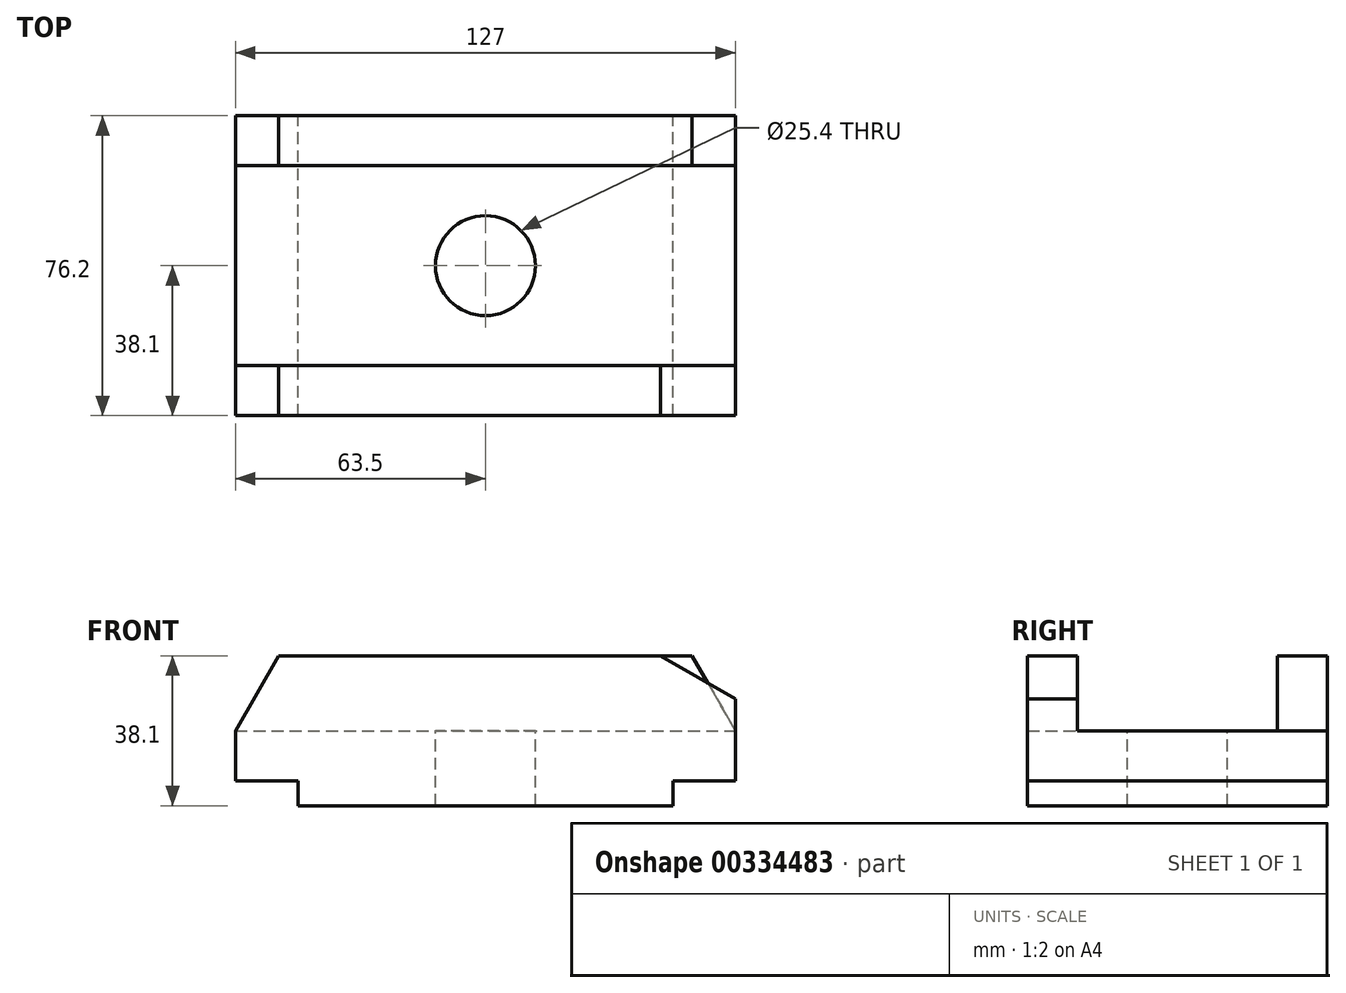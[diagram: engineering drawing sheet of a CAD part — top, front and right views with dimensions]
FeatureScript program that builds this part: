
annotation { "Feature Type Name" : "Feature", "Feature Type Description" : "" }
export const myFeature = defineFeature(function(context is Context, id is Id, definition is map)
    precondition{}
    {
        {
            var Q0;
            Q0=qCreatedBy(makeId("Front.planeOp"),FACE);
            var sketch = newSketch(context, id + "F0", { "sketchPlane" : qUnion([Q0])});
            skLineSegment(sketch, "E0", {"start": v(15.87, 0) * mm, "end": v(111.12, 0) * mm});
            skLineSegment(sketch, "E1", {"start": v(111.12, 0) * mm, "end": v(111.12, 6.35) * mm});
            skLineSegment(sketch, "E2", {"start": v(15.87, 0) * mm, "end": v(15.87, 6.35) * mm});
            skLineSegment(sketch, "E3", {"start": v(15.87, 6.35) * mm, "end": v(0, 6.35) * mm});
            skLineSegment(sketch, "E4", {"start": v(0, 6.35) * mm, "end": v(0, 19.05) * mm});
            skLineSegment(sketch, "E5", {"start": v(111.12, 6.35) * mm, "end": v(127, 6.35) * mm});
            skLineSegment(sketch, "E6", {"start": v(127, 6.35) * mm, "end": v(127, 19.05) * mm});
            skLineSegment(sketch, "E7", {"start": v(127, 19.05) * mm, "end": v(127, 38.1) * mm});
            skLineSegment(sketch, "E8", {"start": v(127, 38.1) * mm, "end": v(0, 38.1) * mm});
            skLineSegment(sketch, "E9", {"start": v(0, 38.1) * mm, "end": v(0, 19.05) * mm});
            skSolve(sketch);
        }
        {
            var Q0;
            Q0=makeQuery(id+"F0.imprint","IMPRINT",FACE,{"disambiguationData":[TD([[makeQuery(id+"F0.imprint","IMPRINT",EDGE,{"derivedFrom":sQuery(id+"F0.wireOp",EDGE,"E0")}),1.0]])]});
            extrude(context, id + "F1", {"entities" : qUnion([Q0]), "depth" : 76.2 * mm});
        }
        {
            var Q0;
            Q0=makeQuery(id+"F1.opExtrude","SWEPT_FACE",FACE,{"disambiguationData":[OSD([sQuery(id+"F0.wireOp",EDGE,"E8")])]});
            var sketch = newSketch(context, id + "F2", { "sketchPlane" : qUnion([Q0])});
            skLineSegment(sketch, "E10", {"start": v(0, -12.7) * mm, "end": v(127, -12.7) * mm});
            skLineSegment(sketch, "E11", {"start": v(0, -63.5) * mm, "end": v(127, -63.5) * mm});
            skSolve(sketch);
        }
        {
            var Q0;
            Q0 = qSketchRegion(id + "F2", true);
            var Q1;
            {var subQ0=sQuery(id+"F2.wireOp",EDGE,"E10");Q1=makeQuery(id+"F2.imprint","IMPRINT",FACE,{"disambiguationData":[TD([[makeQuery(id+"F2.imprint","IMPRINT",EDGE,{"derivedFrom":subQ0}),-1.0]])]});}
            extrude(context, id + "F3", {"entities" : qUnion([Q0, Q1]), "operationType" : NewBodyOperationType.REMOVE, "oppositeDirection" : true, "depth" : 19.05 * mm});
        }
        {
            var Q0;
            {var subQ0=sQuery(id+"F0.wireOp",EDGE,"E9");var subQ1=sQuery(id+"F0.wireOp",EDGE,"E8");Q0=makeQuery(id+"F3.boolean.opBoolean","SPLIT",EDGE,{"disambiguationData":[TD([makeQuery(id+"F3.opExtrude","SWEPT_FACE",FACE,{"disambiguationData":[OSD([sQuery(id+"F2.wireOp",EDGE,"E10")])]})])],"derivedFrom":makeQuery(id+"F1.opExtrude","SWEPT_EDGE",EDGE,{"disambiguationData":[OSD([subQ1,subQ0])]})});}
            var Q1;
            {var subQ0=sQuery(id+"F0.wireOp",EDGE,"E8");var subQ1=sQuery(id+"F0.wireOp",EDGE,"E7");Q1=makeQuery(id+"F3.boolean.opBoolean","SPLIT",EDGE,{"disambiguationData":[TD([makeQuery(id+"F3.opExtrude","SWEPT_FACE",FACE,{"disambiguationData":[OSD([sQuery(id+"F2.wireOp",EDGE,"E10")])]})])],"derivedFrom":makeQuery(id+"F1.opExtrude","SWEPT_EDGE",EDGE,{"disambiguationData":[OSD([subQ1,subQ0])]})});}
            var Q2;
            {var subQ0=sQuery(id+"F0.wireOp",EDGE,"E8");var subQ1=sQuery(id+"F0.wireOp",EDGE,"E7");Q2=makeQuery(id+"F3.boolean.opBoolean","SPLIT",EDGE,{"disambiguationData":[TD([makeQuery(id+"F3.opExtrude","SWEPT_FACE",FACE,{"disambiguationData":[OSD([sQuery(id+"F2.wireOp",EDGE,"E11")])]})])],"derivedFrom":makeQuery(id+"F1.opExtrude","SWEPT_EDGE",EDGE,{"disambiguationData":[OSD([subQ1,subQ0])]})});}
            var Q3;
            {var subQ0=sQuery(id+"F0.wireOp",EDGE,"E9");var subQ1=sQuery(id+"F0.wireOp",EDGE,"E8");Q3=makeQuery(id+"F3.boolean.opBoolean","SPLIT",EDGE,{"disambiguationData":[TD([makeQuery(id+"F3.opExtrude","SWEPT_FACE",FACE,{"disambiguationData":[OSD([sQuery(id+"F2.wireOp",EDGE,"E11")])]})])],"derivedFrom":makeQuery(id+"F1.opExtrude","SWEPT_EDGE",EDGE,{"disambiguationData":[OSD([subQ1,subQ0])]})});}
            chamfer(context, id + "F4", {"entities" : qUnion([Q0, Q1, Q2, Q3]), "chamferType" : ChamferType.OFFSET_ANGLE, "width" : 19.05 * mm, "oppositeDirection" : false, "angle" : 30 * degree, "tangentPropagation" : true});
        }
        {
            var Q0;
            Q0=makeQuery(id+"F3.boolean.opBoolean","COPY",FACE,{"derivedFrom":makeQuery(id+"F3.opExtrude","CAP_FACE",FACE,{"disambiguationData":[OSD([sQuery(id+"F0.wireOp",EDGE,"E7"),sQuery(id+"F0.wireOp",EDGE,"E8"),sQuery(id+"F0.wireOp",EDGE,"E9"),sQuery(id+"F2.wireOp",EDGE,"E10"),sQuery(id+"F2.wireOp",EDGE,"E11")])],"isStart":false})});
            var sketch = newSketch(context, id + "F5", { "sketchPlane" : qUnion([Q0])});
            skLineSegment(sketch, "E12", {"start": v(127, -12.7) * mm, "end": v(63.5, -12.7) * mm});
            skLineSegment(sketch, "E13", {"start": v(63.5, -12.7) * mm, "end": v(63.5, -38.1) * mm});
            skCircle(sketch, "E14", {"center": v(63.5, -38.1) * mm, "radius": 12.7 * mm});
            skSolve(sketch);
        }
        {
            var Q0;
            Q0=makeQuery(id+"F5.imprint","IMPRINT",FACE,{"disambiguationData":[TD([[makeQuery(id+"F5.imprint","IMPRINT",EDGE,{"derivedFrom":sQuery(id+"F5.wireOp",EDGE,"E14")}),1.0]])]});
            extrude(context, id + "F6", {"entities" : qUnion([Q0]), "operationType" : NewBodyOperationType.REMOVE, "oppositeDirection" : true, "depth" : 56.64 * mm});
        }
    });
